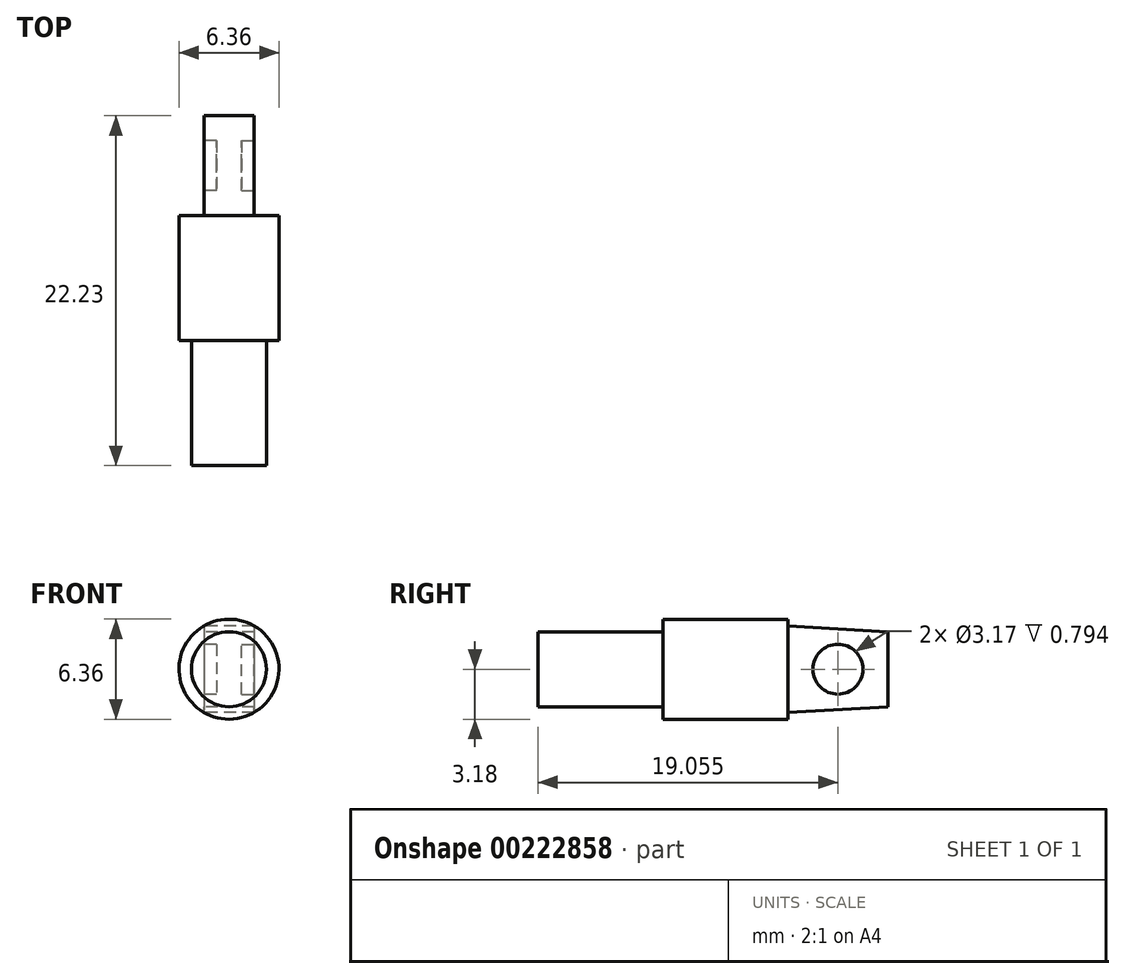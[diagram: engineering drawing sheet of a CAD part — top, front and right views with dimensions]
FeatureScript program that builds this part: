
annotation { "Feature Type Name" : "Feature", "Feature Type Description" : "" }
export const myFeature = defineFeature(function(context is Context, id is Id, definition is map)
    precondition{}
    {
        {
            var Q0;
            Q0=qCreatedBy(makeId("Front.planeOp"),FACE);
            var sketch = newSketch(context, id + "F0", { "sketchPlane" : qUnion([Q0])});
            skCircle(sketch, "E0", {"center": v(0, 0) * mm, "radius": 3.18 * mm});
            skCircle(sketch, "E1", {"center": v(0, 0) * mm, "radius": 2.38 * mm});
            skSolve(sketch);
        }
        {
            var Q0;
            Q0 = qSketchRegion(id + "F0", true);
            extrude(context, id + "F1", {"entities" : qUnion([Q0]), "depth" : 7.94 * mm});
        }
        {
            var Q0;
            Q0=makeQuery(id+"F0.imprint","IMPRINT",FACE,{"disambiguationData":[TD([[makeQuery(id+"F0.imprint","IMPRINT",EDGE,{"derivedFrom":sQuery(id+"F0.wireOp",EDGE,"E1")}),1.0]])]});
            extrude(context, id + "F2", {"entities" : qUnion([Q0]), "operationType" : NewBodyOperationType.ADD, "depth" : 15.88 * mm});
        }
        {
            var Q0;
            {var subQ0=sQuery(id+"F0.wireOp",EDGE,"E1");Q0=makeQuery(id+"F2.boolean.opBoolean","MERGE",FACE,{"derivedFrom":[makeQuery(id+"F1.opExtrude","CAP_FACE",FACE,{"disambiguationData":[OSD([sQuery(id+"F0.wireOp",EDGE,"E0"),subQ0])],"isStart":true}),makeQuery(id+"F2.opExtrude","CAP_FACE",FACE,{"disambiguationData":[OSD([subQ0])],"isStart":true})]});}
            var sketch = newSketch(context, id + "F3", { "sketchPlane" : qUnion([Q0])});
            skPoint(sketch, "E2.middle", {"position": v(0, 0) * mm});
            skLineSegment(sketch, "E3.bottom", {"start": v(-1.59, 2.75) * mm, "end": v(1.59, 2.75) * mm});
            skLineSegment(sketch, "E3.top", {"start": v(-1.59, -2.75) * mm, "end": v(1.59, -2.75) * mm});
            skLineSegment(sketch, "E3.left", {"start": v(-1.59, 2.75) * mm, "end": v(-1.59, -2.75) * mm});
            skLineSegment(sketch, "E3.right", {"start": v(1.59, 2.75) * mm, "end": v(1.59, -2.75) * mm});
            skSolve(sketch);
        }
        {
            var Q0;
            Q0=makeQuery(id+"F3.imprint","IMPRINT",FACE,{"disambiguationData":[TD([[makeQuery(id+"F3.imprint","IMPRINT",EDGE,{"derivedFrom":sQuery(id+"F3.wireOp",EDGE,"E3.bottom")}),-1.0]])]});
            cPlane(context, id + "F4", {"entities" : qUnion([Q0]), "cplaneType" : CPlaneType.OFFSET, "offset" : 6.35 * mm, "width" : 152.4 * mm, "height" : 152.4 * mm});
        }
        {
            var Q0;
            Q0=qCreatedBy(id+"F4.planeOp",FACE);
            var sketch = newSketch(context, id + "F5", { "sketchPlane" : qUnion([Q0])});
            skLineSegment(sketch, "E4.bottom", {"start": v(-1.59, 2.38) * mm, "end": v(1.59, 2.38) * mm});
            skLineSegment(sketch, "E4.top", {"start": v(-1.59, -2.38) * mm, "end": v(1.59, -2.38) * mm});
            skLineSegment(sketch, "E4.left", {"start": v(-1.59, 2.38) * mm, "end": v(-1.59, -2.38) * mm});
            skLineSegment(sketch, "E4.right", {"start": v(1.59, 2.38) * mm, "end": v(1.59, -2.38) * mm});
            skPoint(sketch, "E4.middle", {"position": v(0, 0) * mm});
            skSolve(sketch);
        }
        {
            var Q1;
            Q1=makeQuery(id+"F3.imprint","IMPRINT",FACE,{"disambiguationData":[TD([[makeQuery(id+"F3.imprint","IMPRINT",EDGE,{"derivedFrom":sQuery(id+"F3.wireOp",EDGE,"E3.bottom")}),-1.0]])]});
            var Q2;
            Q2=makeQuery(id+"F5.imprint","IMPRINT",FACE,{"disambiguationData":[TD([[makeQuery(id+"F5.imprint","IMPRINT",EDGE,{"derivedFrom":sQuery(id+"F5.wireOp",EDGE,"E4.bottom")}),-1.0]])]});
            loft(context, id + "F6", {"operationType" : NewBodyOperationType.ADD, "sheetProfilesArray" : [{ "sheetProfileEntities" : qUnion([Q1]) }, { "sheetProfileEntities" : qUnion([Q2]) }]});
        }
        {
            var Q0;
            Q0=makeQuery(id+"F6.opLoft","SWEPT_FACE",FACE,{"disambiguationData":[OSD([sQuery(id+"F0.wireOp",EDGE,"E0"),sQuery(id+"F3.wireOp",EDGE,"E3.bottom"),sQuery(id+"F3.wireOp",EDGE,"E3.top"),sQuery(id+"F3.wireOp",EDGE,"E3.left"),sQuery(id+"F5.wireOp",EDGE,"E4.bottom"),sQuery(id+"F5.wireOp",EDGE,"E4.top"),sQuery(id+"F5.wireOp",EDGE,"E4.left")])]});
            var sketch = newSketch(context, id + "F7", { "sketchPlane" : qUnion([Q0])});
            skPoint(sketch, "E5.centerSnap0", {"position": v(6.35, 0) * mm});
            skCircle(sketch, "E6", {"center": v(3.18, 0) * mm, "radius": 1.59 * mm});
            skSolve(sketch);
        }
        {
            var Q0;
            Q0=makeQuery(id+"F7.imprint","IMPRINT",FACE,{"disambiguationData":[TD([[makeQuery(id+"F7.imprint","IMPRINT",EDGE,{"derivedFrom":sQuery(id+"F7.wireOp",EDGE,"E6")}),1.0]])]});
            extrude(context, id + "F8", {"entities" : qUnion([Q0]), "operationType" : NewBodyOperationType.REMOVE, "oppositeDirection" : true, "depth" : 0.8 * mm});
        }
        {
            var Q0;
            Q0=makeQuery(id+"F6.opLoft","SWEPT_FACE",FACE,{"disambiguationData":[OSD([sQuery(id+"F0.wireOp",EDGE,"E0"),sQuery(id+"F3.wireOp",EDGE,"E3.bottom"),sQuery(id+"F3.wireOp",EDGE,"E3.top"),sQuery(id+"F3.wireOp",EDGE,"E3.right"),sQuery(id+"F5.wireOp",EDGE,"E4.bottom"),sQuery(id+"F5.wireOp",EDGE,"E4.top"),sQuery(id+"F5.wireOp",EDGE,"E4.right")])]});
            var sketch = newSketch(context, id + "F9", { "sketchPlane" : qUnion([Q0])});
            skCircle(sketch, "E7", {"center": v(-3.18, 0) * mm, "radius": 1.59 * mm});
            skPoint(sketch, "E7.centerSnap0", {"position": v(-6.35, 0) * mm});
            skSolve(sketch);
        }
        {
            var Q0;
            Q0 = qSketchRegion(id + "F9", true);
            extrude(context, id + "F10", {"entities" : qUnion([Q0]), "operationType" : NewBodyOperationType.REMOVE, "oppositeDirection" : true, "depth" : 0.8 * mm});
        }
    });
